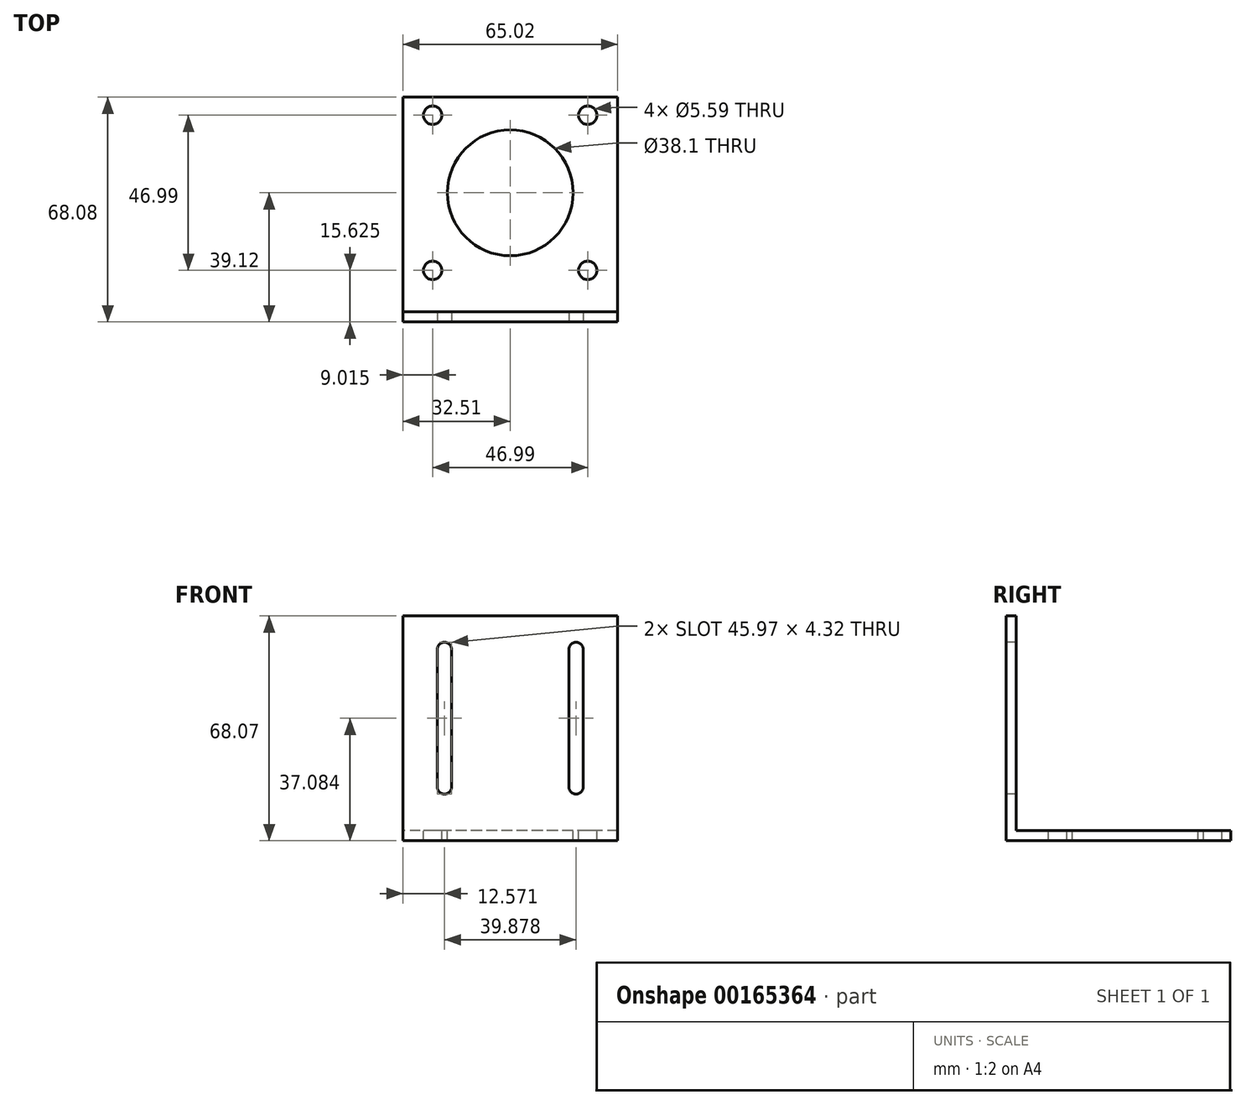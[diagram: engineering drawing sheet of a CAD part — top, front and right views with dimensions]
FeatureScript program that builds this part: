
annotation { "Feature Type Name" : "Feature", "Feature Type Description" : "" }
export const myFeature = defineFeature(function(context is Context, id is Id, definition is map)
    precondition{}
    {
        {
            var Q0;
            Q0=qCreatedBy(makeId("Top.planeOp"),FACE);
            var sketch = newSketch(context, id + "F0", { "sketchPlane" : qUnion([Q0])});
            skLineSegment(sketch, "E0.rect.bottom", {"start": v(32.51, 34.04) * mm, "end": v(-32.51, 34.04) * mm});
            skLineSegment(sketch, "E0.rect.top", {"start": v(32.51, -34.04) * mm, "end": v(-32.51, -34.04) * mm});
            skLineSegment(sketch, "E0.rect.left", {"start": v(32.51, 34.04) * mm, "end": v(32.51, -34.04) * mm});
            skLineSegment(sketch, "E0.rect.right", {"start": v(-32.51, 34.04) * mm, "end": v(-32.51, -34.04) * mm});
            skPoint(sketch, "E0.rect.middle", {"position": v(0, 0) * mm});
            skSolve(sketch);
        }
        {
            var Q0;
            Q0=qSketchRegion(id+"F0",true);
            extrude(context, id + "F1", {"entities" : qUnion([Q0]), "depth" : 68.07 * mm});
        }
        {
            var Q0;
            Q0=makeQuery(id+"F1.opExtrude","CAP_FACE",FACE,{"disambiguationData":[OSD([sQuery(id+"F0.wireOp",EDGE,"E0.rect.bottom"),sQuery(id+"F0.wireOp",EDGE,"E0.rect.top"),sQuery(id+"F0.wireOp",EDGE,"E0.rect.left"),sQuery(id+"F0.wireOp",EDGE,"E0.rect.right")])],"isStart":false});
            var sketch = newSketch(context, id + "F2", { "sketchPlane" : qUnion([Q0])});
            skLineSegment(sketch, "E1.bottom", {"start": v(-32.51, 34.04) * mm, "end": v(32.51, 34.04) * mm});
            skLineSegment(sketch, "E1.top", {"start": v(-32.51, -30.99) * mm, "end": v(32.51, -30.99) * mm});
            skLineSegment(sketch, "E1.left", {"start": v(-32.51, 34.04) * mm, "end": v(-32.51, -30.99) * mm});
            skLineSegment(sketch, "E1.right", {"start": v(32.51, 34.04) * mm, "end": v(32.51, -30.99) * mm});
            skSolve(sketch);
        }
        {
            var Q0;
            Q0=qSketchRegion(id+"F2",true);
            extrude(context, id + "F3", {"entities" : qUnion([Q0]), "operationType" : NewBodyOperationType.REMOVE, "oppositeDirection" : true, "depth" : 65.02 * mm});
        }
        {
            var Q0;
            Q0=makeQuery(id+"F3.boolean.opBoolean","COPY",FACE,{"derivedFrom":makeQuery(id+"F3.opExtrude","CAP_FACE",FACE,{"disambiguationData":[OSD([sQuery(id+"F2.wireOp",EDGE,"E1.bottom"),sQuery(id+"F2.wireOp",EDGE,"E1.top"),sQuery(id+"F2.wireOp",EDGE,"E1.left"),sQuery(id+"F2.wireOp",EDGE,"E1.right")])],"isStart":false})});
            var sketch = newSketch(context, id + "F4", { "sketchPlane" : qUnion([Q0])});
            skLineSegment(sketch, "E2", {"start": v(32.51, 5.08) * mm, "end": v(-32.51, 5.08) * mm, "construction": true});
            skCircle(sketch, "E3", {"center": v(0, 5.08) * mm, "radius": 19.05 * mm});
            skLineSegment(sketch, "E4", {"start": v(0, 34.04) * mm, "end": v(0, -34.3) * mm, "construction": true});
            skLineSegment(sketch, "E5.rect.bottom", {"start": v(23.5, -18.41) * mm, "end": v(-23.5, -18.42) * mm, "construction": true});
            skLineSegment(sketch, "E5.rect.top", {"start": v(23.5, 28.58) * mm, "end": v(-23.5, 28.57) * mm, "construction": true});
            skLineSegment(sketch, "E5.rect.left", {"start": v(23.5, -18.41) * mm, "end": v(23.5, 28.58) * mm, "construction": true});
            skLineSegment(sketch, "E5.rect.right", {"start": v(-23.5, -18.42) * mm, "end": v(-23.5, 28.57) * mm, "construction": true});
            skCircle(sketch, "E6", {"center": v(-23.5, 28.57) * mm, "radius": 2.8 * mm});
            skCircle(sketch, "E7", {"center": v(23.5, 28.58) * mm, "radius": 2.8 * mm});
            skCircle(sketch, "E8", {"center": v(23.5, -18.41) * mm, "radius": 2.8 * mm});
            skCircle(sketch, "E9", {"center": v(-23.5, -18.42) * mm, "radius": 2.8 * mm});
            skSolve(sketch);
        }
        {
            var Q0;
            Q0=qSketchRegion(id+"F4",true);
            extrude(context, id + "F5", {"entities" : qUnion([Q0]), "operationType" : NewBodyOperationType.REMOVE, "endBound" : BoundingType.THROUGH_ALL, "oppositeDirection" : true, "depth" : 25.4 * mm});
        }
        {
            var Q0;
            Q0=makeQuery(id+"F1.opExtrude","SWEPT_FACE",FACE,{"disambiguationData":[OSD([sQuery(id+"F0.wireOp",EDGE,"E0.rect.top")])]});
            var sketch = newSketch(context, id + "F6", { "sketchPlane" : qUnion([Q0])});
            skLineSegment(sketch, "E10", {"start": v(-32.51, 57.91) * mm, "end": v(32.51, 57.91) * mm, "construction": true});
            skLineSegment(sketch, "E11", {"start": v(0, 0) * mm, "end": v(0, 68.07) * mm, "construction": true});
            skLineSegment(sketch, "E12", {"start": v(-19.94, 0) * mm, "end": v(-19.94, 68.07) * mm, "construction": true});
            skLineSegment(sketch, "E13", {"start": v(19.94, 0) * mm, "end": v(19.94, 68.07) * mm, "construction": true});
            skLineSegment(sketch, "E14", {"start": v(-32.51, 16.26) * mm, "end": v(32.51, 16.26) * mm, "construction": true});
            skLineSegment(sketch, "E15", {"start": v(32.51, 16.26) * mm, "end": v(32.37, 15.84) * mm, "construction": true});
            skLineSegment(sketch, "E16", {"start": v(-32.51, 37.08) * mm, "end": v(32.51, 37.08) * mm, "construction": true});
            skLineSegment(sketch, "E17.rect.left", {"start": v(-22.1, 57.91) * mm, "end": v(-22.1, 16.26) * mm});
            skLineSegment(sketch, "E17.rect.right", {"start": v(-17.78, 57.91) * mm, "end": v(-17.78, 16.26) * mm});
            skPoint(sketch, "E17.rect.middle", {"position": v(-19.94, 37.08) * mm});
            skLineSegment(sketch, "E18.rect.left", {"start": v(17.78, 57.91) * mm, "end": v(17.78, 16.26) * mm});
            skLineSegment(sketch, "E18.rect.right", {"start": v(22.1, 57.91) * mm, "end": v(22.1, 16.26) * mm});
            skPoint(sketch, "E18.rect.middle", {"position": v(19.94, 37.08) * mm});
            skArc(sketch, "E19", {"start": v(-22.1, 16.26) * mm, "mid": v(-19.94, 14.1) * mm, "end": v(-17.78, 16.26) * mm});
            skArc(sketch, "E20", {"start": v(-17.78, 57.91) * mm, "mid": v(-19.94, 60.07) * mm, "end": v(-22.1, 57.91) * mm});
            skArc(sketch, "E21", {"start": v(17.78, 16.26) * mm, "mid": v(19.94, 14.1) * mm, "end": v(22.1, 16.26) * mm});
            skArc(sketch, "E22", {"start": v(22.1, 57.91) * mm, "mid": v(19.94, 60.07) * mm, "end": v(17.78, 57.91) * mm});
            skSolve(sketch);
        }
        {
            var Q0;
            Q0=qSketchRegion(id+"F6",true);
            extrude(context, id + "F7", {"entities" : qUnion([Q0]), "operationType" : NewBodyOperationType.REMOVE, "endBound" : BoundingType.THROUGH_ALL, "oppositeDirection" : true, "depth" : 25.4 * mm});
        }
    });
